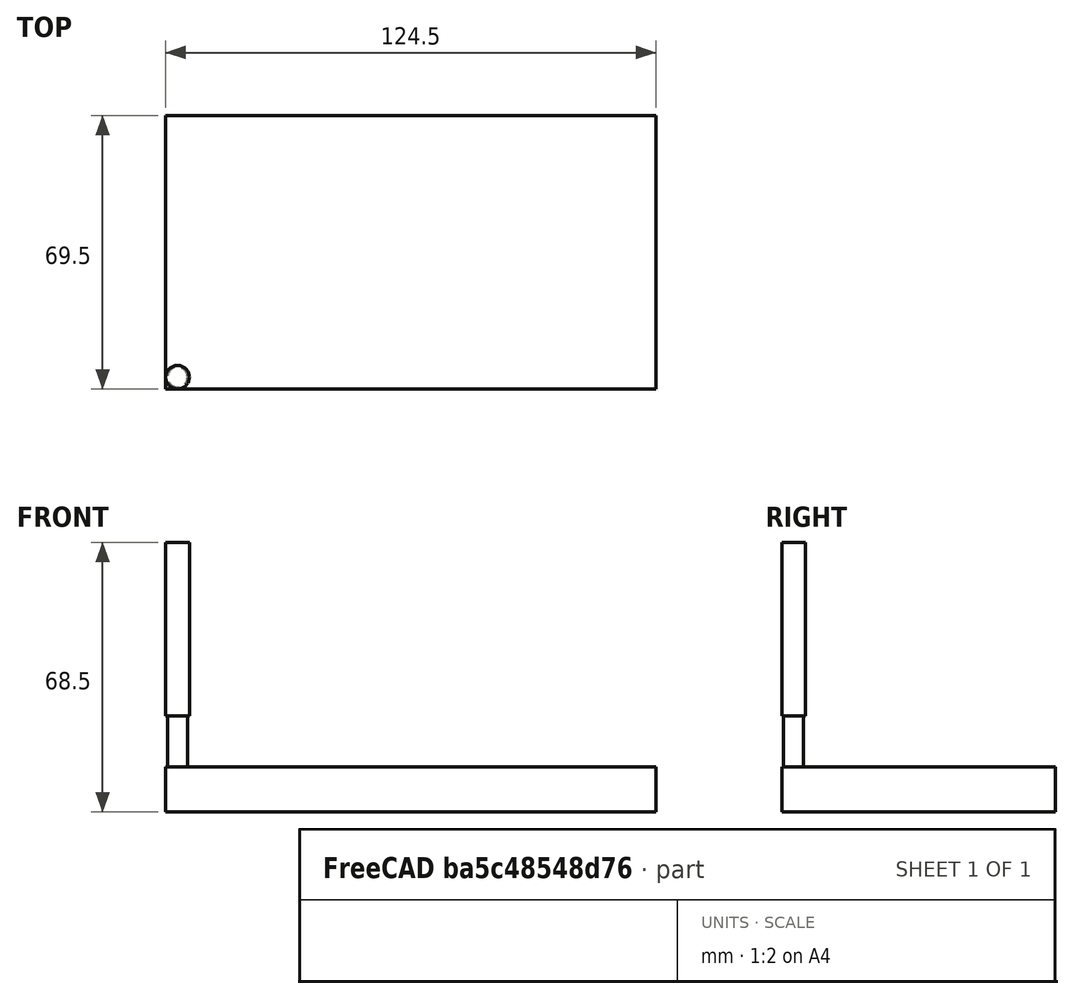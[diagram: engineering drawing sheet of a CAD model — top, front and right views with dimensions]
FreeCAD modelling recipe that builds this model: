
FCSTD DOCUMENT  (FreeCAD 0.21R33771 (Git))
Label: kumiko_box_floor
License: All rights reserved
LicenseURL: https://en.wikipedia.org/wiki/All_rights_reserved
objects: Path::FeaturePython×4, Part::FeaturePython×3, App::DocumentObjectGroup×3, Sketcher::SketchObject×2, PartDesign::Pad×2, App::Link×1, PartDesign::Body×1, App::FeaturePython×1, Mesh::FeaturePython×1
note: 12 computed .brp shape members not serialized (recipe doc carries the construction recipe); baked Part::Feature solids carry a one-line shape summary decoded from their .brp
EXTERNAL_REF file=../../master_kumiko_box.FCStd obj=Spreadsheet

FEATURE [App::Link] Link  label="SpreadSheet"
  LinkedObject = -> <external ../../master_kumiko_box.FCStd>#Spreadsheet
FEATURE [Sketcher::SketchObject] Sketch  label="ground_pad_drawing"
  FullyConstrained = true
  MapMode = 5
  Support = -> [XY_Plane043]
  expr: Constraints[10] = <<SpreadSheet>>.box_width - 2 * <<SpreadSheet>>.box_thickness
  expr: Constraints[11] = <<SpreadSheet>>.box_length - 2 * <<SpreadSheet>>.box_thickness
  expr: Constraints[8] = <<SpreadSheet>>.box_thickness / 2
  expr: Constraints[9] = <<SpreadSheet>>.box_thickness / 2
  sketch-geometry (4):
    g0: LineSegment StartX=5.75 StartY=5.75 StartZ=0 EndX=112.75 EndY=5.75 EndZ=0
    g1: LineSegment StartX=112.75 StartY=5.75 StartZ=0 EndX=112.75 EndY=57.75 EndZ=0
    g2: LineSegment StartX=112.75 StartY=57.75 StartZ=0 EndX=5.75 EndY=57.75 EndZ=0
    g3: LineSegment StartX=5.75 StartY=57.75 StartZ=0 EndX=5.75 EndY=5.75 EndZ=0
  constraints (12):
    c: Coincident(g0,g1)
    c: Coincident(g1,g2)
    c: Coincident(g2,g3)
    c: Coincident(g3,g0)
    c: Horizontal(g0)
    c: Horizontal(g2)
    c: Vertical(g1)
    c: Vertical(g3)
    c: DistanceX(g-1,g0) = 5.75
    c: DistanceY(g-1,g0) = 5.75
    c: DistanceY(g3,g3) = 52
    c: DistanceX(g2,g2) = 107
FEATURE [PartDesign::Pad] Pad  label="ground_pad"
  Direction = (0,0,1)
  Length = 5.75
  Length2 = 10
  Profile = -> Sketch
  ReferenceAxis = -> Sketch [N_Axis]
  Type = 0
  expr: Length = <<SpreadSheet>>.box_thickness / 2
FEATURE [Sketcher::SketchObject] Sketch001  label="half_lap_joint_drawing"
  FullyConstrained = true
  MapMode = 5
  Placement = pos=(0,0,5.75) rot=(0,0,1;0rad)
  Support = -> [Pad]
  expr: Constraints[10] = <<SpreadSheet>>.box_width - <<SpreadSheet>>.box_thickness
  expr: Constraints[9] = <<SpreadSheet>>.box_length - <<SpreadSheet>>.box_thickness
  sketch-geometry (4):
    g0: LineSegment StartX=0 StartY=0 StartZ=0 EndX=118.5 EndY=0 EndZ=0
    g1: LineSegment StartX=118.5 StartY=0 StartZ=0 EndX=118.5 EndY=63.5 EndZ=0
    g2: LineSegment StartX=118.5 StartY=63.5 StartZ=0 EndX=0 EndY=63.5 EndZ=0
    g3: LineSegment StartX=0 StartY=63.5 StartZ=0 EndX=0 EndY=0 EndZ=0
  constraints (12):
    c: Coincident(g0,g1)
    c: Coincident(g1,g2)
    c: Coincident(g2,g3)
    c: Coincident(g3,g0)
    c: Horizontal(g0)
    c: Horizontal(g2)
    c: Vertical(g1)
    c: Vertical(g3)
    c: PointOnObject(g0,g-1)
    c: DistanceX(g2,g2) = 118.5
    c: DistanceY(g1,g1) = 63.5
    c: DistanceX(g-1,g0) = 0
FEATURE [PartDesign::Pad] Pad001  label="half_lap_jount"
  BaseFeature = -> Pad
  Direction = (0,0,1)
  Length = 5.75
  Length2 = 10
  Profile = -> Sketch001
  ReferenceAxis = -> Sketch001 [N_Axis]
  Type = 0
  expr: Length = <<SpreadSheet>>.box_thickness / 2
FEATURE [PartDesign::Body] Body032  label="floor_body"
  Group = -> [Sketch,Pad,Sketch001,Pad001]
  Origin = -> Origin043
  Placement = pos=(0,63.5,0) rot=(1,0,0;3.14159rad)
  Tip = -> Pad001
  expr: .Placement.Base.x = 0
  expr: .Placement.Base.y = <<SpreadSheet>>.box_width - <<SpreadSheet>>.box_thickness
  expr: .Placement.Base.z = 0
FEATURE [App::FeaturePython] SetupSheet  # Path/CAM operation (typed FeaturePython)
  ClearanceHeightExpression = OpStockZMax+SetupSheet.ClearanceHeightOffset
  ClearanceHeightOffset = 5
  CoolantMode = 0
  CoolantModes = None | Flood | Mist
  FinalDepthExpression = OpFinalDepth
  HorizRapid = 0
  SafeHeightExpression = OpStockZMax+SetupSheet.SafeHeightOffset
  SafeHeightOffset = 3
  StartDepthExpression = OpStartDepth
  StepDownExpression = OpToolDiameter
  VertRapid = 0
FEATURE [Part::FeaturePython] Clone  label="Model-floor_body"  # Draft clone (typed FeaturePython)
  AttacherType = Attacher::AttachEngine3D
  Fuse = false
  Objects = -> [Body032]
  PathResource = Model
  Placement = pos=(0,63.5,0) rot=(1,0,0;3.14159rad)
  Scale = (1,1,1)
FEATURE [App::DocumentObjectGroup] Model
  Group = -> [Clone]
FEATURE [Part::FeaturePython] Stock  # WARN: FeaturePython — macro-defined, semantics opaque (R4)
  Base = -> Model
  ExtXneg = 3
  ExtXpos = 3
  ExtYneg = 3
  ExtYpos = 3
  ExtZneg = 0
  ExtZpos = 0
  Placement = pos=(0,0,-11.5) rot=(0,0,1;0rad)
  StockType = FromBase
FEATURE [Part::FeaturePython] ToolBit001  label="FREES_5mm"  # Path/CAM toolbit (typed FeaturePython)
  BitPropertyNames = Chipload | CuttingEdgeHeight | Diameter | Flutes | Length | Material | ShankDiameter | SpindleDirection
  BitShape = /Applications/FreeCAD.app/Contents/Resources/Mod/Path/Tools/Shape/endmill.fcstd
  Chipload = 0
  CuttingEdgeHeight = 13
  Diameter = 5
  File = <userpath>/Library/Application Support/FreeCAD/Macro/FREES_5mm.fctb
  Flutes = 0
  Length = 57
  Material = 0
  ShankDiameter = 6
  ShapeName = endmill
  SpindleDirection = 0
FEATURE [Path::FeaturePython] FREES_5mm  label="FREES_5mm001"  # Path/CAM operation (typed FeaturePython)
  HorizFeed = 1
  HorizRapid = 0
  SpindleDir = 0
  SpindleSpeed = 4
  Tool = -> ToolBit001
  ToolNumber = 2
  VertFeed = 0.5
  VertRapid = 0
  expr: HorizRapid = SetupSheet.HorizRapid
  expr: VertRapid = SetupSheet.VertRapid
FEATURE [App::DocumentObjectGroup] Tools
  Group = -> [FREES_5mm]
FEATURE [Path::FeaturePython] Profile  # Path/CAM operation (typed FeaturePython)
  Active = true
  AreaParams:
    Tolerance = 1e-07
    FitArcs = True
    Simplify = False
    CleanDistance = 0.0
    Accuracy = 0.01
    Unit = 1.0
    MinArcPoints = 4
    MaxArcPoints = 100
    ClipperScale = 10000000.0
    Fill = 0
    Coplanar = 0
    Reorient = True
    Outline = False
    Explode = False
    OpenMode = 0
    Deflection = 0.01
    SubjectFill = 0
    ClipFill = 0
    Offset = 2.5
    ExtraPass = 0
    Stepover = 0.0
    LastStepover = 0.0
    JoinType = 0
    EndType = 0
    MiterLimit = 2.0
    RoundPrecision = 0.0
    PocketMode = 0
    ToolRadius = 1.0
    PocketExtraOffset = 0.0
    PocketStepover = 0.0
    PocketLastStepover = 0.0
    FromCenter = False
    Angle = 45.0
    AngleShift = 0.0
    Shift = 0.0
    Thicken = False
    SectionCount = -1
    Stepdown = 1.0
    SectionOffset = 0.0
    SectionTolerance = 1e-07
    SectionMode = 2
    Project = False
  Base = -> [Clone]
  ClearanceHeight = 5
  CoolantMode = 0
  CycleTime = 01:16:33
  Direction = 1
  FinalDepth = -11.5
  HandleMultipleFeatures = 0
  JoinType = 0
  MiterLimit = 0.1
  OffsetExtra = 0
  OpFinalDepth = -11.5
  OpStartDepth = 7.1e-15
  OpStockZMax = 0
  OpStockZMin = -11.5
  OpToolDiameter = 5
  PathParams = {'orientation': 0, 'feedrate': 1.0, 'feedrate_v': 0.5, 'verbose': True, 'resume_height': 3.0, 'retraction': 5.0, 'return_end': True, 'preamble': False, 'start': Vector (0.0, 0.0, 0.0)}
  SafeHeight = 3
  Side = 0
  SplitArcs = false
  StartDepth = 7.1e-15
  StartPoint = (0,0,0)
  StepDown = 1
  ToolController = -> FREES_5mm
  UseComp = true
  UseStartPoint = true
  processCircles = false
  processHoles = false
  processPerimeter = true
  expr: ClearanceHeight = OpStockZMax + SetupSheet.ClearanceHeightOffset
  expr: FinalDepth = OpFinalDepth
  expr: SafeHeight = OpStockZMax + SetupSheet.SafeHeightOffset
  expr: StartDepth = OpStartDepth
  expr: StepDown = 1
FEATURE [Path::FeaturePython] Pocket_Shape  # Path/CAM operation (typed FeaturePython)
  Active = true
  AreaParams:
    Tolerance = 1e-07
    FitArcs = True
    Simplify = False
    CleanDistance = 0.0
    Accuracy = 0.01
    Unit = 1.0
    MinArcPoints = 4
    MaxArcPoints = 100
    ClipperScale = 10000000.0
    Fill = 0
    Coplanar = 0
    Reorient = True
    Outline = False
    Explode = False
    OpenMode = 0
    Deflection = 0.01
    SubjectFill = 0
    ClipFill = 0
    Offset = 0.0
    ExtraPass = 0
    Stepover = 0.0
    LastStepover = 0.0
    JoinType = 0
    EndType = 0
    MiterLimit = 2.0
    RoundPrecision = 0.0
    PocketMode = 2
    ToolRadius = 2.5
    PocketExtraOffset = 0.0
    PocketStepover = 2.0
    PocketLastStepover = 0.0
    FromCenter = True
    Angle = 45.0
    AngleShift = 0.0
    Shift = 0.0
    Thicken = False
    SectionCount = -1
    Stepdown = 1.0
    SectionOffset = 0.0
    SectionTolerance = 1e-07
    SectionMode = 2
    Project = False
  Base = -> [Clone]
  ClearanceHeight = 5
  CoolantMode = 0
  CutMode = 0
  CycleTime = 02:11:12
  ExtensionCorners = true
  ExtensionFeature = -> [Clone]
  ExtensionLengthDefault = 2.5
  ExtraOffset = 0
  FinalDepth = -5.75
  FinishDepth = 0.5
  KeepToolDown = false
  MinTravel = false
  OffsetPattern = 1
  OpFinalDepth = -5.75
  OpStartDepth = 7.1e-15
  OpStockZMax = 0
  OpStockZMin = -11.5
  OpToolDiameter = 5
  PathParams = {'orientation': 1, 'feedrate': 1.0, 'feedrate_v': 0.5, 'verbose': True, 'resume_height': 3.0, 'retraction': 5.0, 'return_end': True, 'preamble': False, 'start': Vector (0.0, 0.0, 0.0)}
  PocketLastStepOver = 0
  SafeHeight = 3
  SplitArcs = false
  StartAt = 0
  StartDepth = 7.1e-15
  StartPoint = (0,0,0)
  StepDown = 1
  StepOver = 40
  ToolController = -> FREES_5mm
  UseOutline = false
  UseStartPoint = true
  ZigZagAngle = 45
  expr: ClearanceHeight = OpStockZMax + SetupSheet.ClearanceHeightOffset
  expr: ExtensionLengthDefault = OpToolDiameter / 2
  expr: FinalDepth = OpFinalDepth
  expr: SafeHeight = OpStockZMax + SetupSheet.SafeHeightOffset
  expr: StartDepth = OpStartDepth
  expr: StepDown = 1
FEATURE [App::DocumentObjectGroup] Operations
  Group = -> [Profile,Pocket_Shape]
FEATURE [Path::FeaturePython] Job  # Path/CAM operation (typed FeaturePython)
  CycleTime = 03:27:45
  Fixtures = G54
  GeometryTolerance = 0.01
  JobType = 0
  LastPostProcessDate = 2024-03-20 12:44:18.073578
  LastPostProcessOutput = <userpath>/Documents/jewelry_kumiko_box/cnc/bin/kumiko_floor-0.nc
  Model = -> Model
  Operations = -> Operations
  OrderOutputBy = 0
  PostProcessor = 14
  PostProcessorOutputFile = <userpath>/Documents/jewelry_kumiko_box/cnc/bin/kumiko_floor.nc
  SetupSheet = -> SetupSheet
  SplitOutput = true
  Stock = -> Stock
  Tools = -> Tools
FEATURE [Mesh::FeaturePython] CutMaterial  # WARN: FeaturePython — macro-defined, semantics opaque (R4)
